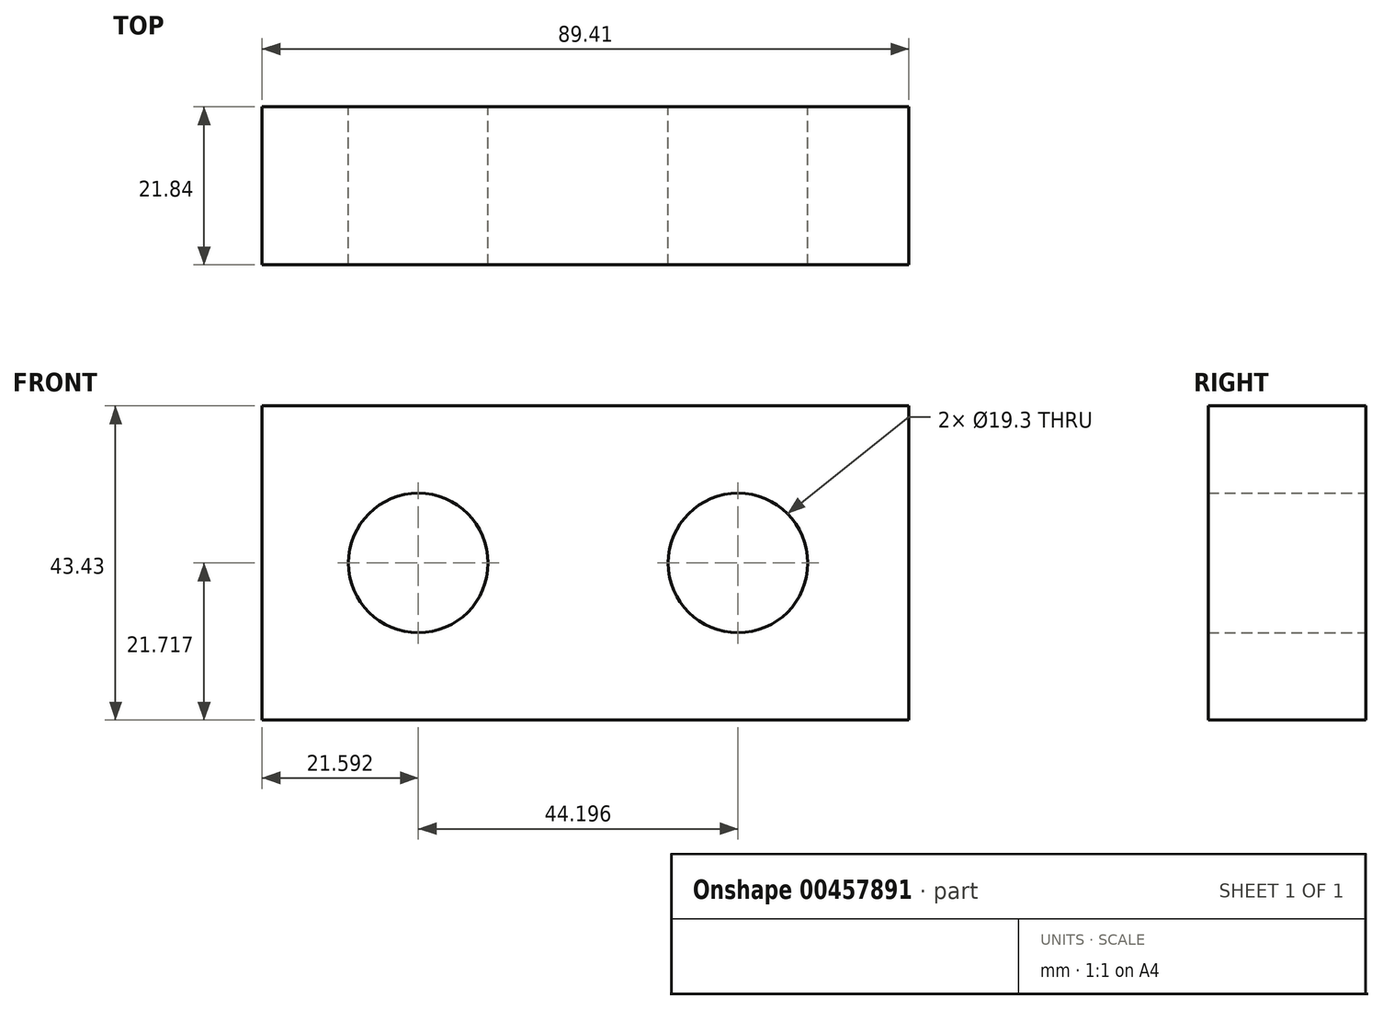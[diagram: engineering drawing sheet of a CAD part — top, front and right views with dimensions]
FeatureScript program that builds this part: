
annotation { "Feature Type Name" : "Feature", "Feature Type Description" : "" }
export const myFeature = defineFeature(function(context is Context, id is Id, definition is map)
    precondition{}
    {
        {
            var Q0;
            Q0=qCreatedBy(makeId("Front.planeOp"),FACE);
            var sketch = newSketch(context, id + "F0", { "sketchPlane" : qUnion([Q0])});
            skPoint(sketch, "E0.0", {"position": v(0, 0) * mm});
            skLineSegment(sketch, "E1", {"start": v(0, 0) * mm, "end": v(-89.4, 0) * mm});
            skLineSegment(sketch, "E2", {"start": v(-89.4, 0) * mm, "end": v(-89.4, 43.43) * mm});
            skLineSegment(sketch, "E3", {"start": v(-89.4, 43.43) * mm, "end": v(0, 43.43) * mm});
            skLineSegment(sketch, "E4", {"start": v(0, 43.43) * mm, "end": v(0, 0) * mm});
            skLineSegment(sketch, "E5", {"start": v(0, 0) * mm, "end": v(0, 0) * mm});
            skCircle(sketch, "E6", {"center": v(-67.82, 21.72) * mm, "radius": 9.65 * mm});
            skCircle(sketch, "E7", {"center": v(-23.62, 21.72) * mm, "radius": 9.65 * mm});
            skSolve(sketch);
        }
        {
            var Q0;
            Q0 = qSketchRegion(id + "F0", true);
            extrude(context, id + "F1", {"entities" : qUnion([Q0]), "depth" : 21.84 * mm, "offsetDistance" : 25.4 * mm});
        }
    });
